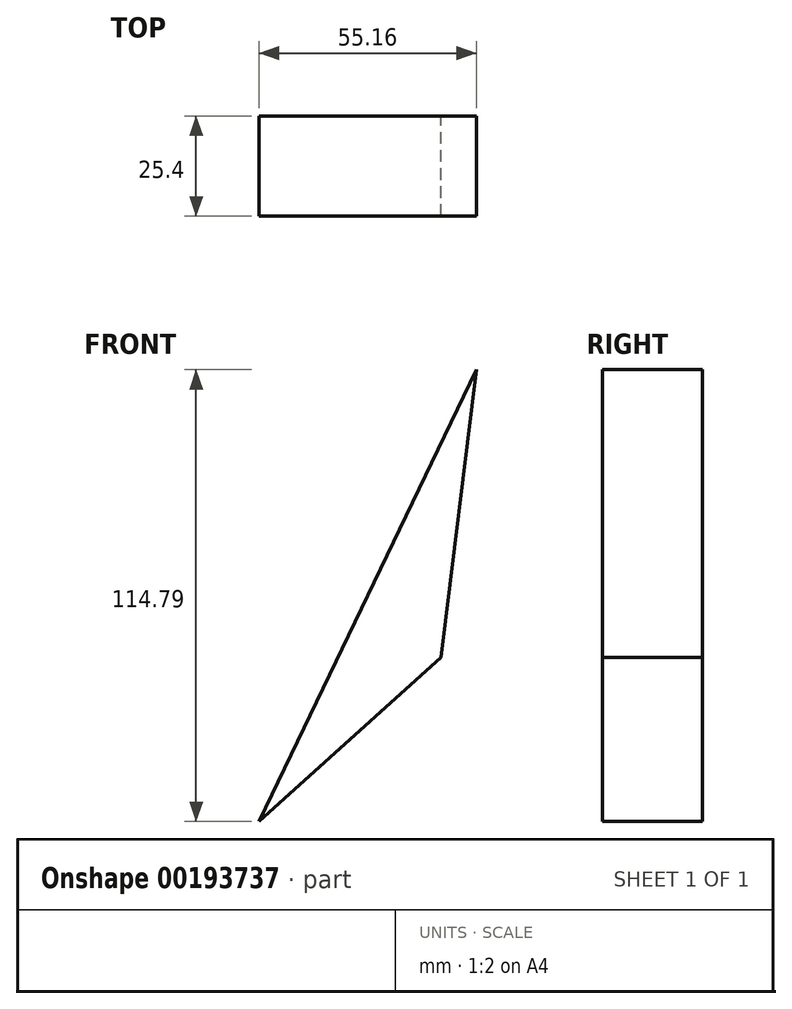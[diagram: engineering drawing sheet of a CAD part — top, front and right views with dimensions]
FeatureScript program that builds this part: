
annotation { "Feature Type Name" : "Feature", "Feature Type Description" : "" }
export const myFeature = defineFeature(function(context is Context, id is Id, definition is map)
    precondition{}
    {
        {
            var Q0;
            Q0=qCreatedBy(makeId("Front.planeOp"),FACE);
            var sketch = newSketch(context, id + "F0", { "sketchPlane" : qUnion([Q0])});
            skLineSegment(sketch, "E0", {"start": v(25.08, 41.45) * mm, "end": v(25.8, 50.61) * mm});
            skLineSegment(sketch, "E1", {"start": v(25.8, 50.61) * mm, "end": v(16.84, -22.54) * mm});
            skLineSegment(sketch, "E2", {"start": v(16.84, -22.54) * mm, "end": v(-29.37, -64.18) * mm});
            skLineSegment(sketch, "E3", {"start": v(-29.37, -64.18) * mm, "end": v(25.8, 50.61) * mm});
            skSolve(sketch);
        }
        {
            var Q0;
            Q0 = qSketchRegion(id + "F0", true);
            extrude(context, id + "F1", {"entities" : qUnion([Q0]), "depth" : 25.4 * mm});
        }
    });
